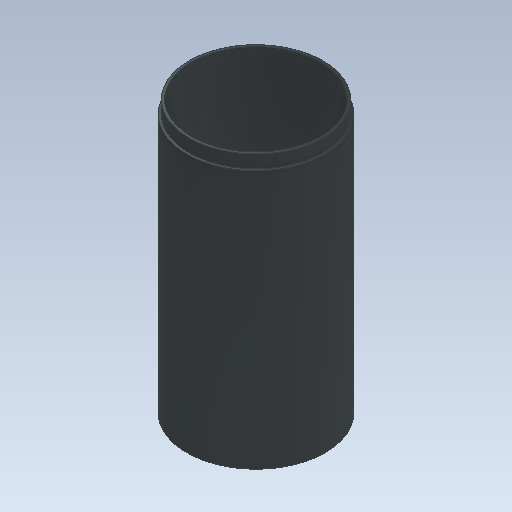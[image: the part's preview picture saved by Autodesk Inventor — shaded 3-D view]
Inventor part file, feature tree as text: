
AUTODESK INVENTOR PART (.ipt)
format: ipt  version: 2020.3 (Build 243373000, 373)  size: 110,080 bytes
history: native  units: mm
features: extrude x2, sketch x1
ambient origin geometry x8: Origin, YZ Plane, XZ Plane, XY Plane, X Axis, Y Axis, Z Axis, Center Point
bodies: Solid1 (feature_tree)
feature tree (3):
  sketch  "Sketch1"  dims[d0=51.8mm d1=50.0mm d2=53.6mm d3=100.0mm d4=0.0mm d5=45.0mm d6=55.0mm d7=0.0mm d8=0.0mm]
  extrude  "Extrusion1"  Depth=100.0mm TaperAngle=0.0deg
  extrude  "Extrusion2"  Depth=45.0mm TaperAngle=0.0deg
